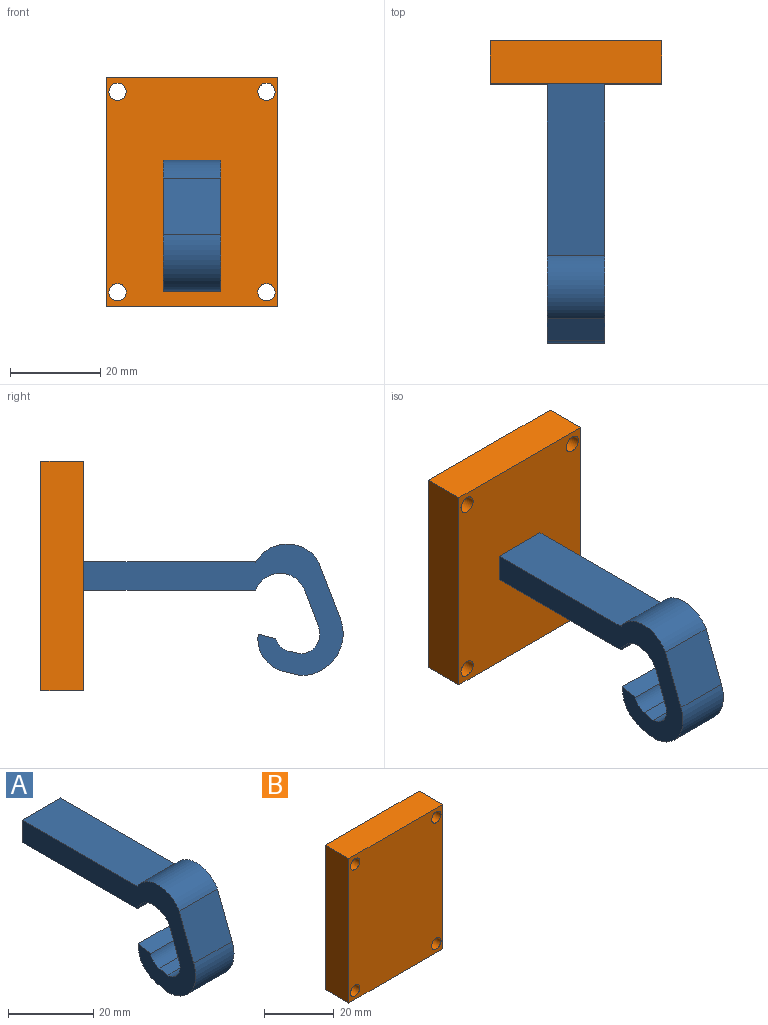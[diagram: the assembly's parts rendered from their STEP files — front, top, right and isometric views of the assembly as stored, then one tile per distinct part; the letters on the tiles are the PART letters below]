
ASSEMBLY  parts=2 mates=1
PART A: 17 faces, bbox 12.7x57.5x29.2 mm
  f0: plane 12.7x0.07mm, normal (0,-1,0), area 0.9mm2, adj f1,f14,f15,f16
  f1: cylinder r=8.1mm len=13.96mm, axis (-1,0,0), area 213.7mm2, adj f0,f2,f15,f16
  f2: plane 12.7x12.58mm, normal (0,-0.93,0.36), area 171.2mm2, adj f1,f3,f15,f16
  f3: cylinder r=9.26mm len=12.7mm, axis (-1,0,0), area 229.1mm2, adj f2,f4,f15,f16
  f4: plane 12.7x3.84mm, normal (0,0.23,-0.97), area 50.1mm2, adj f3,f5,f15,f16
  f5: cylinder r=7.4mm len=12.7mm, axis (-1,0,0), area 140mm2, adj f4,f6,f15,f16
  f6: plane 12.7x3.83mm, normal (0,-0.27,0.96), area 50.4mm2, adj f5,f7,f15,f16
  f7: cylinder r=3.92mm len=12.7mm, axis (-1,0,0), area 52.3mm2, adj f6,f8,f15,f16
  f8: plane 12.7x2.78mm, normal (0,-0.23,0.97), area 36.2mm2, adj f7,f9,f15,f16
  f9: cylinder r=4.42mm len=12.7mm, axis (-1,0,0), area 105.7mm2, adj f8,f10,f15,f16
  f10: plane 12.7x8.13mm, normal (0,0.94,-0.35), area 110.3mm2, adj f9,f11,f15,f16
  f11: cylinder r=5.82mm len=12.7mm, axis (-1,0,0), area 179.1mm2, adj f10,f12,f15,f16
  f12: plane 38.1x12.7mm, normal (0,0,-1), area 483.9mm2, adj f11,f13,f15,f16
  f13: plane 12.7x6.35mm, normal (0,1,0), area 80.6mm2, adj f12,f14,f15,f16
  f14: plane 38.1x12.7mm, normal (0,0,1), area 483.9mm2, adj f0,f13,f15,f16
  f15: plane 57.5x29.15mm, normal (1,0,0), area 501.4mm2, adj f0,f1,f2,f3,f4,f5,f6,f7
  f16: plane 57.5x29.15mm, normal (-1,0,0), area 501.4mm2, adj f0,f1,f2,f3,f4,f5,f6,f7
PART B: 10 faces, bbox 38.1x9.5x50.8 mm
  f0: plane 50.8x9.53mm, normal (-1,0,0), area 483.9mm2, adj f1,f7,f8,f9
  f1: plane 38.1x9.53mm, normal (0,0,-1), area 362.9mm2, adj f0,f2,f8,f9
  f2: plane 50.8x9.53mm, normal (1,0,0), area 483.9mm2, adj f1,f7,f8,f9
  f3: cylinder r=1.91mm len=9.53mm, axis (0,1,0), area 114mm2, adj f8,f9
  f4: cylinder r=1.91mm len=9.53mm, axis (0,1,0), area 114mm2, adj f8,f9
  f5: cylinder r=1.91mm len=9.53mm, axis (0,1,0), area 114mm2, adj f8,f9
  f6: cylinder r=1.91mm len=9.53mm, axis (0,1,0), area 114mm2, adj f8,f9
  f7: plane 38.1x9.53mm, normal (0,0,1), area 362.9mm2, adj f0,f2,f8,f9
  f8: plane 50.8x38.1mm, normal (0,-1,0), area 1889.9mm2, adj f0,f1,f2,f3,f4,f5,f6,f7
  f9: plane 50.8x38.1mm, normal (0,1,0), area 1889.9mm2, adj f0,f1,f2,f3,f4,f5,f6,f7
PLACE A t=(7.22,21.56,5.49)mm
PLACE B t=(7.22,7.79,5.44)mm
MATE fastened A.f13 <-> B.f8  axis (0,1,0) through (7.22,3.03,5.44)mm
